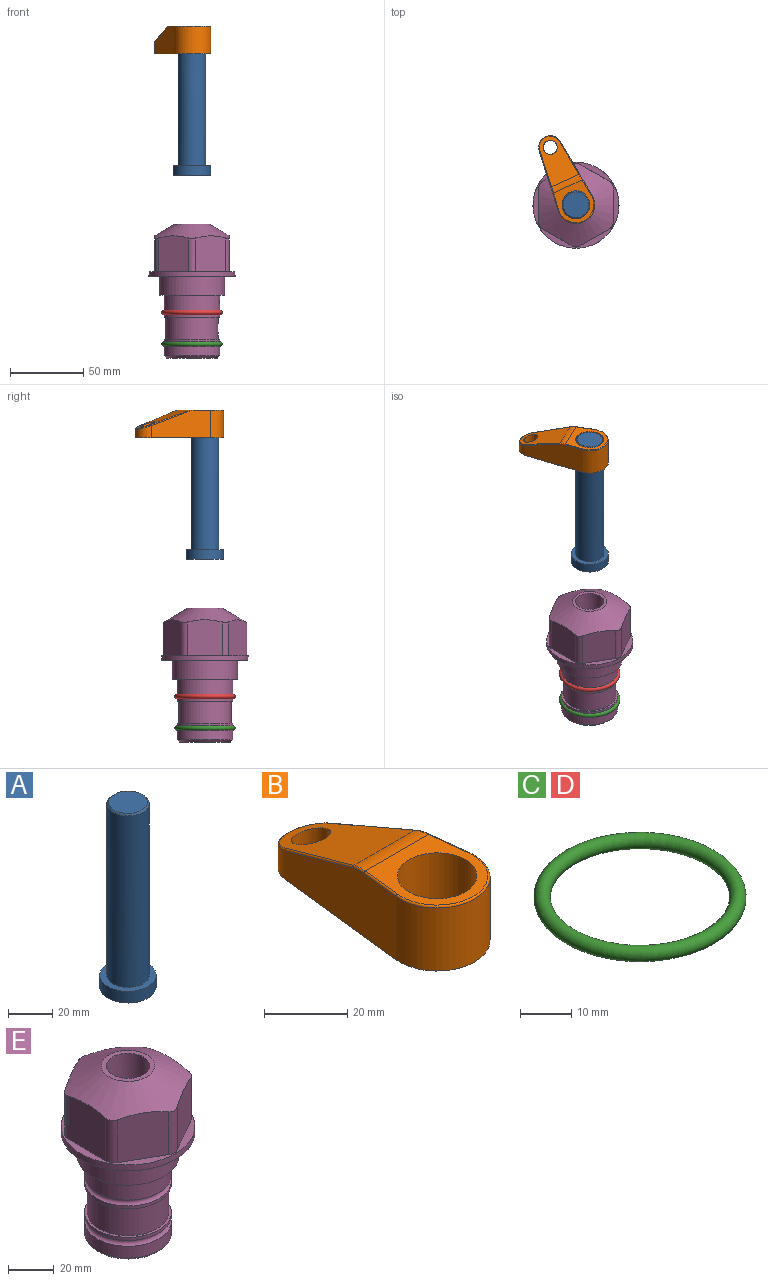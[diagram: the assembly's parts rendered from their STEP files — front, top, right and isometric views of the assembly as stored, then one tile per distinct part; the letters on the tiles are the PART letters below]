
ASSEMBLY  parts=5 mates=3
PART A: 6 faces, bbox 25.4x25.4x101.6 mm
  f0: plane 17.46x17.46mm, normal (0,0,1), area 239.5mm2, adj f5
  f1: plane 25.4x25.4mm, normal (0,0,-1), area 506.7mm2, adj f2
  f2: cylinder r=12.7mm len=25.4mm, axis (0,0,1), area 506.7mm2, adj f1,f3
  f3: plane 25.4x25.4mm, normal (0,0,1), area 221.7mm2, adj f2,f4
  f4: cylinder r=9.53mm len=94.46mm, axis (0,0,1), area 5653mm2, adj f3,f5
  f5: cone r=8.73mm half-angle=45deg, axis (0,0,-1), area 64.4mm2, adj f0,f4
PART B: 44 faces, bbox 27.5x64.5x19.1 mm
  f0: plane 2.3x0.95mm, normal (0,0,-1), area 1mm2, adj f25,f30,f34
  f1: plane 63.5x25.4mm, normal (0,0,-1), area 561.7mm2, adj f2,f3,f4,f5,f6,f7,f19,f20
  f2: cylinder r=12.7mm len=25.4mm, axis (0,0,-1), area 792.2mm2, adj f1,f3,f5,f13
  f3: plane 42.33x18.54mm, normal (0.99,0.11,0), area 647mm2, adj f1,f2,f4,f11,f12,f14
  f4: cylinder r=7.94mm len=15.78mm, axis (0,0,-1), area 158.6mm2, adj f1,f3,f5,f16
  f5: plane 42.33x18.54mm, normal (-0.99,0.11,0), area 647mm2, adj f1,f2,f4,f15,f17,f18
  f6: cylinder r=9.53mm len=19.05mm, axis (0,0,-1), area 1140.1mm2, adj f1,f8
  f7: cylinder r=4.76mm len=10.98mm, axis (0,0,-1), area 276.1mm2, adj f1,f9
  f8: plane 25.83x24.38mm, normal (0,0,1), area 262.2mm2, adj f6,f10,f11,f13,f15
  f9: plane 32.49x20.55mm, normal (0,0.34,0.94), area 489.9mm2, adj f7,f10,f14,f16,f18
  f10: cylinder r=12.7mm len=21.49mm, axis (-1,0,0), area 93.2mm2, adj f8,f9,f12,f17
  f11: cylinder r=0.51mm len=12.34mm, axis (0.11,-0.99,0), area 9.9mm2, adj f3,f8,f12,f13
  f12: bspline ~7.62x1.64mm, area 3.5mm2, adj f3,f10,f11,f14
  f13: torus R=12.19mm, axis (0,0,1), area 33.6mm2, adj f2,f8,f11,f15
  f14: cylinder r=0.51mm len=26.01mm, axis (0.1,-0.93,0.34), area 21.6mm2, adj f3,f9,f12,f16
  f15: cylinder r=0.51mm len=12.34mm, axis (0.11,0.99,0), area 9.9mm2, adj f5,f8,f13,f17
  f16: bspline ~15.78x7.05mm, area 15.7mm2, adj f4,f9,f14,f18
  f17: bspline ~7.62x1.64mm, area 3.5mm2, adj f5,f10,f15,f18
  f18: cylinder r=0.51mm len=26.01mm, axis (0.1,0.93,-0.34), area 21.6mm2, adj f5,f9,f16,f17
  f19: plane 21.6x14.29mm, normal (-0.99,-0.11,0), area 242.6mm2, adj f1,f26,f28,f34,f36,f38
  f20: plane 21.6x14.29mm, normal (0.99,-0.11,0), area 242.6mm2, adj f1,f27,f29,f37,f39,f41
  f21: cylinder r=12.7mm len=14.29mm, axis (0,0,-1), area 173.2mm2, adj f1,f26,f27,f30,f31,f33
  f22: cylinder r=7.94mm len=7.63mm, axis (0,0,-1), area 53.8mm2, adj f1,f28,f29,f42
  f23: plane 2.3x0.95mm, normal (0,0,-1), area 1mm2, adj f25,f33,f37
  f24: plane 17.94x12.32mm, normal (0,-0.34,-0.94), area 191.2mm2, adj f25,f38,f41,f42
  f25: cylinder r=9.53mm len=12.93mm, axis (-1,0,0), area 37.5mm2, adj f0,f23,f24,f31,f36,f39
  f26: cylinder r=1.59mm len=14.29mm, axis (0,0,-1), area 49mm2, adj f1,f19,f21,f32
  f27: cylinder r=1.59mm len=14.29mm, axis (0,0,-1), area 49mm2, adj f1,f20,f21,f35
  f28: cylinder r=1.59mm len=7.28mm, axis (0,0,-1), area 22.1mm2, adj f1,f19,f22,f40
  f29: cylinder r=1.59mm len=7.28mm, axis (0,0,-1), area 22.1mm2, adj f1,f20,f22,f43
  f30: torus R=14.29mm, axis (0,0,1), area 5.8mm2, adj f0,f21,f31,f32
  f31: bspline ~11.06x2.73mm, area 20.8mm2, adj f21,f25,f30,f33
  f32: sphere r=1.59mm, area 5.4mm2, adj f26,f30,f34
  f33: torus R=14.29mm, axis (0,0,1), area 5.8mm2, adj f21,f23,f31,f35
  f34: cylinder r=1.59mm len=1.68mm, axis (-0.11,0.99,0), area 2.4mm2, adj f0,f19,f32,f36
  f35: sphere r=1.59mm, area 5.4mm2, adj f27,f33,f37
  f36: bspline ~5.82x2.33mm, area 7.7mm2, adj f19,f25,f34,f38
  f37: cylinder r=1.59mm len=1.68mm, axis (0.11,0.99,0), area 2.4mm2, adj f20,f23,f35,f39
  f38: cylinder r=1.59mm len=18.33mm, axis (0.1,-0.93,0.34), area 46.7mm2, adj f19,f24,f36,f40
  f39: bspline ~5.82x2.33mm, area 7.7mm2, adj f20,f25,f37,f41
  f40: sphere r=1.59mm, area 3.6mm2, adj f28,f38,f42
  f41: cylinder r=1.59mm len=18.33mm, axis (0.1,0.93,-0.34), area 46.7mm2, adj f20,f24,f39,f43
  f42: bspline ~8.31x1.84mm, area 15.3mm2, adj f22,f24,f40,f43
  f43: sphere r=1.59mm, area 3.6mm2, adj f29,f41,f42
PART C: 1 faces, bbox 44.7x44.7x3.2 mm
  f0: torus R=19.05mm, axis (0,0,1), area 1193.9mm2
PART D: same geometry as C
PART E: 36 faces, bbox 58.7x58.7x91.2 mm
  f0: cylinder r=17.78mm len=35.56mm, axis (0,0,1), area 1670.8mm2, adj f23,f24,f31
  f1: cylinder r=19.05mm len=38.1mm, axis (0,0,1), area 1191.9mm2, adj f26,f27,f30
  f2: plane 58.66x58.66mm, normal (0,0,-1), area 1150.6mm2, adj f3,f28
  f3: cylinder r=29.33mm len=58.66mm, axis (0,0,-1), area 585.1mm2, adj f2,f4
  f4: plane 58.66x58.66mm, normal (0,0,1), area 475.9mm2, adj f3,f5,f6,f7,f8,f9,f10,f11
  f5: plane 24.5x20.32mm, normal (-0.5,0.87,0), area 562.8mm2, adj f4,f15,f16,f17
  f6: plane 24.5x20.32mm, normal (0.5,0.87,0), area 562.8mm2, adj f4,f14,f15,f17
  f7: plane 24.5x23.48mm, normal (1,0,0), area 562.8mm2, adj f4,f13,f14,f17
  f8: plane 24.5x20.32mm, normal (0.5,-0.87,0), area 562.8mm2, adj f4,f12,f13,f17
  f9: plane 24.5x20.32mm, normal (-0.5,-0.87,0), area 562.8mm2, adj f4,f11,f12,f17
  f10: plane 24.5x23.48mm, normal (-1,0,0), area 562.8mm2, adj f4,f11,f16,f17
  f11: cylinder r=5.08mm len=23.01mm, axis (0,0,-1), area 121.2mm2, adj f4,f9,f10,f17
  f12: cylinder r=5.08mm len=23.01mm, axis (0,0,-1), area 121.2mm2, adj f4,f8,f9,f17
  f13: cylinder r=5.08mm len=23.01mm, axis (0,0,-1), area 121.2mm2, adj f4,f7,f8,f17
  f14: cylinder r=5.08mm len=23.01mm, axis (0,0,-1), area 121.2mm2, adj f4,f6,f7,f17
  f15: cylinder r=5.08mm len=23.01mm, axis (0,0,-1), area 121.2mm2, adj f4,f5,f6,f17
  f16: cylinder r=5.08mm len=23.01mm, axis (0,0,-1), area 121.2mm2, adj f4,f5,f10,f17
  f17: cone r=11.73mm half-angle=60deg, axis (0,0,-1), area 2071.8mm2, adj f5,f6,f7,f8,f9,f10,f11,f12
  f18: plane 23.46x23.46mm, normal (0,0,1), area 147.4mm2, adj f17,f35
  f19: plane 34.93x34.93mm, normal (0,0,-1), area 958mm2, adj f29
  f20: cylinder r=19.05mm len=38.1mm, axis (0,0,1), area 760.1mm2, adj f21,f29
  f21: torus R=19.05mm, axis (0,0,1), area 565.3mm2, adj f20,f22
  f22: cylinder r=19.05mm len=38.1mm, axis (0,0,1), area 190mm2, adj f21,f23
  f23: plane 38.1x38.1mm, normal (0,0,1), area 146.9mm2, adj f0,f22
  f24: plane 38.1x38.1mm, normal (0,0,-1), area 146.9mm2, adj f0,f25
  f25: cylinder r=19.05mm len=38.1mm, axis (0,0,1), area 190mm2, adj f24,f26
  f26: torus R=19.05mm, axis (0,0,1), area 565.3mm2, adj f1,f25
  f27: plane 44.45x44.45mm, normal (0,0,-1), area 411.7mm2, adj f1,f28
  f28: cylinder r=22.23mm len=44.45mm, axis (0,0,1), area 1773.5mm2, adj f2,f27
  f29: cone r=19.05mm half-angle=45deg, axis (0,0,1), area 257.5mm2, adj f19,f20
  f30: cylinder r=3.17mm len=6.75mm, axis (-1,0,0), area 128mm2, adj f1,f33
  f31: cylinder r=3.17mm len=6.35mm, axis (-1,0,0), area 102.5mm2, adj f0,f33
  f32: plane 25.4x25.4mm, normal (0,0,1), area 506.7mm2, adj f33
  f33: cylinder r=12.7mm len=66.42mm, axis (0,0,-1), area 5236.2mm2, adj f30,f31,f32,f34
  f34: cone r=9.53mm half-angle=30deg, axis (0,0,-1), area 443.4mm2, adj f33,f35
  f35: cylinder r=9.53mm len=19.05mm, axis (0,0,-1), area 849mm2, adj f18,f34
PLACE A rot(axis=(0,0,1),114.2deg) t=(0,0,96.99)mm
PLACE B rot(axis=(0,0,1),24.2deg) t=(0,0,151.6)mm
PLACE C t=(0,0,-21.59)mm
PLACE D at identity
PLACE E at identity fixed
MATE fastened C.f0 <-> E.f0  axis (0,0,1) through (0,0,-46.1)mm
MATE cylindrical A.f2 <-> E.f0  axis (0,0,1) through (0,0,122.63)mm
MATE fastened B.f2 <-> A.f2  axis (0,0,1) through (0,0,170.65)mm
